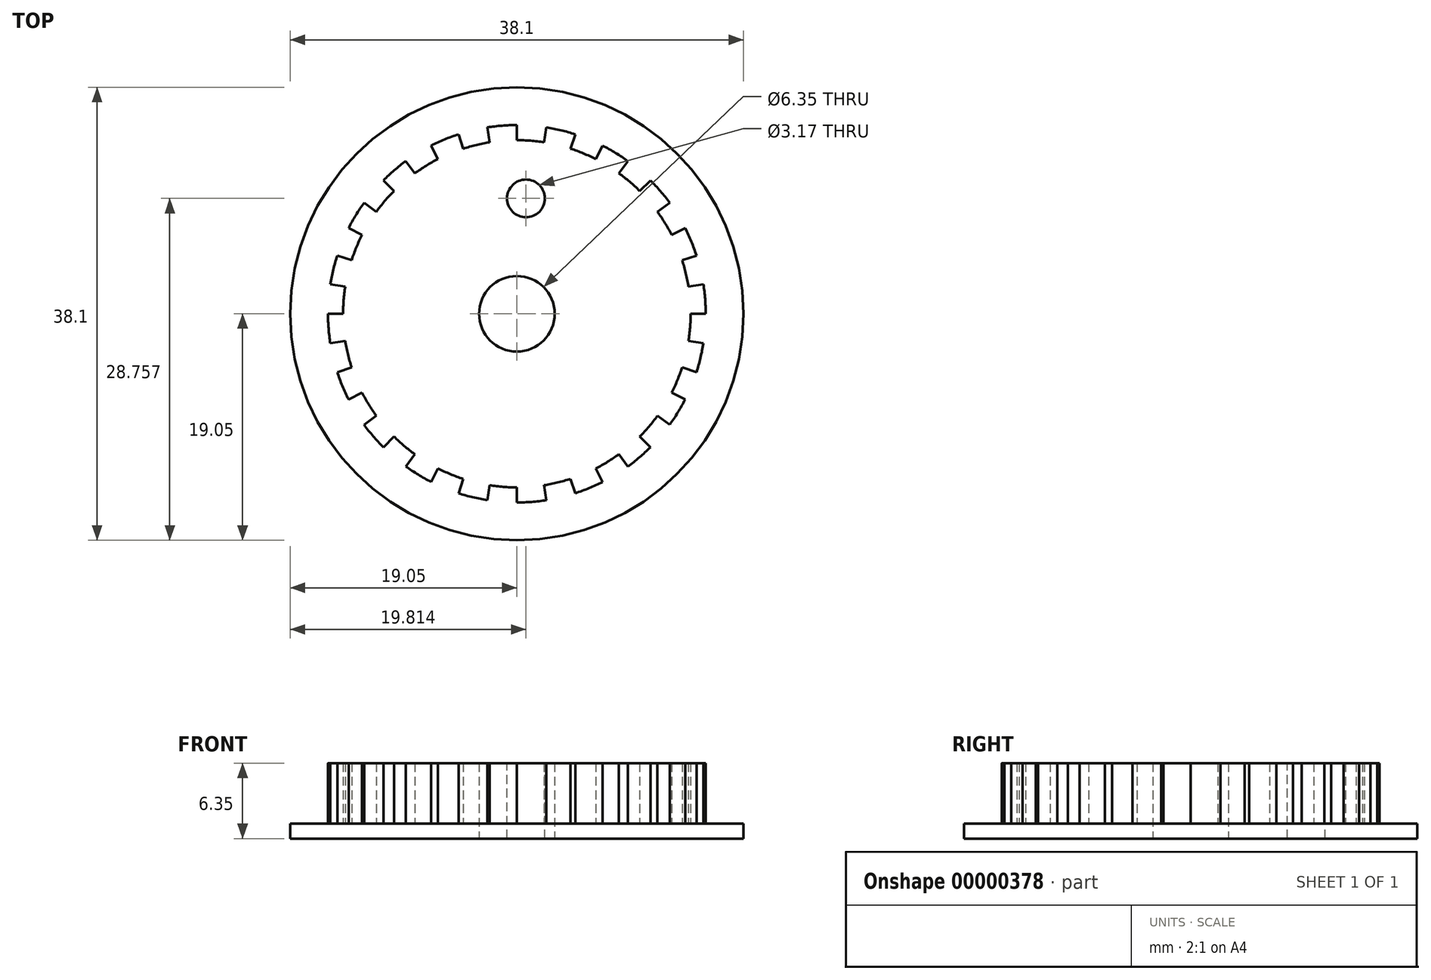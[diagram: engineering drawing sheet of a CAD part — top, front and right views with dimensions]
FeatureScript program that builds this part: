
annotation { "Feature Type Name" : "Feature", "Feature Type Description" : "" }
export const myFeature = defineFeature(function(context is Context, id is Id, definition is map)
    precondition{}
    {
        {
            var Q0;
            Q0  = qCreatedBy(makeId("Top.planeOp"), FACE);
            var sketch = newSketch(context, id + "F0", { "sketchPlane" : qUnion([Q0])});
            skCircle(sketch, "E0", {"center": v(0, 0) * mm, "radius": 19.05 * mm});
            skCircle(sketch, "E1", {"center": v(0, 0) * mm, "radius": 3.18 * mm});
            skSolve(sketch);
        }
        {
            var Q0;
            Q0=makeQuery(id+"F0.imprint","IMPRINT",FACE,{"disambiguationData":[TD([[makeQuery(id+"F0.imprint","IMPRINT",EDGE,{"derivedFrom":sQuery(id+"F0.wireOp",EDGE,"E0")}),1.0]])]});
            extrude(context, id + "F1", {"entities" : qUnion([Q0]), "depth" : 1.27 * mm});
        }
        {
            var Q0;
            Q0=makeQuery(id+"F1.opExtrude","CAP_FACE",FACE,{"disambiguationData":[OSD([sQuery(id+"F0.wireOp",EDGE,"E0"),sQuery(id+"F0.wireOp",EDGE,"E1")])],"isStart":false});
            var sketch = newSketch(context, id + "F2", { "sketchPlane" : qUnion([Q0])});
            skCircle(sketch, "E2", {"center": v(0, 0) * mm, "radius": 14.6 * mm, "construction": true});
            skCircle(sketch, "E3", {"center": v(0, 0) * mm, "radius": 15.88 * mm, "construction": true});
            skLineSegment(sketch, "E4", {"start": v(0, 0) * mm, "end": v(0, 15.88) * mm, "construction": true});
            skLineSegment(sketch, "E5", {"start": v(0, 0) * mm, "end": v(2.48, 15.68) * mm, "construction": true});
            skLineSegment(sketch, "E6", {"start": v(0, 0) * mm, "end": v(4.9, 15.1) * mm, "construction": true});
            skArc(sketch, "E7", {"start": v(2.28, 14.43) * mm, "mid": v(1.15, 14.56) * mm, "end": v(0, 14.6) * mm});
            skLineSegment(sketch, "E8", {"start": v(2.48, 15.68) * mm, "end": v(2.28, 14.43) * mm});
            skArc(sketch, "E9", {"start": v(4.9, 15.1) * mm, "mid": v(3.7, 15.44) * mm, "end": v(2.48, 15.68) * mm});
            skLineSegment(sketch, "E10", {"start": v(0, 14.6) * mm, "end": v(0, 0) * mm});
            skLineSegment(sketch, "E11", {"start": v(4.9, 15.1) * mm, "end": v(0, 0) * mm});
            skSolve(sketch);
        }
        {
            var Q0;
            {var subQ6=sQuery(id+"F2.wireOp",EDGE,"E7");Q0=makeQuery(id+"F2.imprint","IMPRINT",FACE,{"disambiguationData":[TD([[makeQuery(id+"F2.imprint","IMPRINT",EDGE,{"derivedFrom":subQ6}),1.0]])]});}
            var Q1;
            Q1=sQuery(id+"F2.wireOp",EDGE,"E10");
            var Q2;
            Q2=sQuery(id+"F2.wireOp",EDGE,"E7");
            var Q3;
            Q3=sQuery(id+"F2.wireOp",EDGE,"E8");
            var Q4;
            Q4=sQuery(id+"F2.wireOp",EDGE,"E9");
            var Q5;
            Q5=sQuery(id+"F2.wireOp",EDGE,"E11");
            extrude(context, id + "F3", {"entities" : qUnion([Q0]), "surfaceEntities" : qUnion([Q1, Q2, Q3, Q4, Q5]), "depth" : 5.08 * mm});
        }
        {
            var Q0;
            Q0  = qCreatedBy(makeId("Front.planeOp"), FACE);
            var sketch = newSketch(context, id + "F4", { "sketchPlane" : qUnion([Q0])});
            skLineSegment(sketch, "E12", {"start": v(0, 0) * mm, "end": v(0, 20.74) * mm, "construction": true});
            skSolve(sketch);
        }
        {
            var Q0;
            Q0=makeQuery(id+"F3.opExtrude","SWEPT_BODY",BODY,{"disambiguationData":[OSD([sQuery(id+"F0.wireOp",EDGE,"E1"),sQuery(id+"F2.wireOp",EDGE,"E7"),sQuery(id+"F2.wireOp",EDGE,"E8"),sQuery(id+"F2.wireOp",EDGE,"E9"),sQuery(id+"F2.wireOp",EDGE,"E10"),sQuery(id+"F2.wireOp",EDGE,"E11")])]});
            var Q1;
            Q1=sQuery(id+"F4.wireOp",EDGE,"E12");
            circularPattern(context, id + "F5", {"entities" : qUnion([Q0]), "axis" : qUnion([Q1]), "angle" : 18 * degree, "instanceCount" : 20});
        }
        {
            var Q0;
            Q0=makeQuery(id+"F1.opExtrude","SWEPT_BODY",BODY,{"disambiguationData":[OSD([sQuery(id+"F0.wireOp",EDGE,"E0"),sQuery(id+"F0.wireOp",EDGE,"E1")])]});
            var Q1;
            Q1=makeQuery(id+"F5.opPattern","COPY",BODY,{"derivedFrom":makeQuery(id+"F3.opExtrude","SWEPT_BODY",BODY,{"disambiguationData":[OSD([sQuery(id+"F0.wireOp",EDGE,"E1"),sQuery(id+"F2.wireOp",EDGE,"E7"),sQuery(id+"F2.wireOp",EDGE,"E8"),sQuery(id+"F2.wireOp",EDGE,"E9"),sQuery(id+"F2.wireOp",EDGE,"E10"),sQuery(id+"F2.wireOp",EDGE,"E11")])]}),"instanceName":"4"});
            var Q2;
            Q2=makeQuery(id+"F5.opPattern","COPY",BODY,{"derivedFrom":makeQuery(id+"F3.opExtrude","SWEPT_BODY",BODY,{"disambiguationData":[OSD([sQuery(id+"F0.wireOp",EDGE,"E1"),sQuery(id+"F2.wireOp",EDGE,"E7"),sQuery(id+"F2.wireOp",EDGE,"E8"),sQuery(id+"F2.wireOp",EDGE,"E9"),sQuery(id+"F2.wireOp",EDGE,"E10"),sQuery(id+"F2.wireOp",EDGE,"E11")])]}),"instanceName":"3"});
            var Q3;
            Q3=makeQuery(id+"F5.opPattern","COPY",BODY,{"derivedFrom":makeQuery(id+"F3.opExtrude","SWEPT_BODY",BODY,{"disambiguationData":[OSD([sQuery(id+"F0.wireOp",EDGE,"E1"),sQuery(id+"F2.wireOp",EDGE,"E7"),sQuery(id+"F2.wireOp",EDGE,"E8"),sQuery(id+"F2.wireOp",EDGE,"E9"),sQuery(id+"F2.wireOp",EDGE,"E10"),sQuery(id+"F2.wireOp",EDGE,"E11")])]}),"instanceName":"2"});
            var Q4;
            Q4=makeQuery(id+"F5.opPattern","COPY",BODY,{"derivedFrom":makeQuery(id+"F3.opExtrude","SWEPT_BODY",BODY,{"disambiguationData":[OSD([sQuery(id+"F0.wireOp",EDGE,"E1"),sQuery(id+"F2.wireOp",EDGE,"E7"),sQuery(id+"F2.wireOp",EDGE,"E8"),sQuery(id+"F2.wireOp",EDGE,"E9"),sQuery(id+"F2.wireOp",EDGE,"E10"),sQuery(id+"F2.wireOp",EDGE,"E11")])]}),"instanceName":"1"});
            var Q5;
            Q5=makeQuery(id+"F3.opExtrude","SWEPT_BODY",BODY,{"disambiguationData":[OSD([sQuery(id+"F0.wireOp",EDGE,"E1"),sQuery(id+"F2.wireOp",EDGE,"E7"),sQuery(id+"F2.wireOp",EDGE,"E8"),sQuery(id+"F2.wireOp",EDGE,"E9"),sQuery(id+"F2.wireOp",EDGE,"E10"),sQuery(id+"F2.wireOp",EDGE,"E11")])]});
            var Q6;
            Q6=makeQuery(id+"F5.opPattern","COPY",BODY,{"derivedFrom":makeQuery(id+"F3.opExtrude","SWEPT_BODY",BODY,{"disambiguationData":[OSD([sQuery(id+"F0.wireOp",EDGE,"E1"),sQuery(id+"F2.wireOp",EDGE,"E7"),sQuery(id+"F2.wireOp",EDGE,"E8"),sQuery(id+"F2.wireOp",EDGE,"E9"),sQuery(id+"F2.wireOp",EDGE,"E10"),sQuery(id+"F2.wireOp",EDGE,"E11")])]}),"instanceName":"19"});
            var Q7;
            Q7=makeQuery(id+"F5.opPattern","COPY",BODY,{"derivedFrom":makeQuery(id+"F3.opExtrude","SWEPT_BODY",BODY,{"disambiguationData":[OSD([sQuery(id+"F0.wireOp",EDGE,"E1"),sQuery(id+"F2.wireOp",EDGE,"E7"),sQuery(id+"F2.wireOp",EDGE,"E8"),sQuery(id+"F2.wireOp",EDGE,"E9"),sQuery(id+"F2.wireOp",EDGE,"E10"),sQuery(id+"F2.wireOp",EDGE,"E11")])]}),"instanceName":"18"});
            var Q8;
            Q8=makeQuery(id+"F5.opPattern","COPY",BODY,{"derivedFrom":makeQuery(id+"F3.opExtrude","SWEPT_BODY",BODY,{"disambiguationData":[OSD([sQuery(id+"F0.wireOp",EDGE,"E1"),sQuery(id+"F2.wireOp",EDGE,"E7"),sQuery(id+"F2.wireOp",EDGE,"E8"),sQuery(id+"F2.wireOp",EDGE,"E9"),sQuery(id+"F2.wireOp",EDGE,"E10"),sQuery(id+"F2.wireOp",EDGE,"E11")])]}),"instanceName":"17"});
            var Q9;
            Q9=makeQuery(id+"F5.opPattern","COPY",BODY,{"derivedFrom":makeQuery(id+"F3.opExtrude","SWEPT_BODY",BODY,{"disambiguationData":[OSD([sQuery(id+"F0.wireOp",EDGE,"E1"),sQuery(id+"F2.wireOp",EDGE,"E7"),sQuery(id+"F2.wireOp",EDGE,"E8"),sQuery(id+"F2.wireOp",EDGE,"E9"),sQuery(id+"F2.wireOp",EDGE,"E10"),sQuery(id+"F2.wireOp",EDGE,"E11")])]}),"instanceName":"16"});
            var Q10;
            Q10=makeQuery(id+"F5.opPattern","COPY",BODY,{"derivedFrom":makeQuery(id+"F3.opExtrude","SWEPT_BODY",BODY,{"disambiguationData":[OSD([sQuery(id+"F0.wireOp",EDGE,"E1"),sQuery(id+"F2.wireOp",EDGE,"E7"),sQuery(id+"F2.wireOp",EDGE,"E8"),sQuery(id+"F2.wireOp",EDGE,"E9"),sQuery(id+"F2.wireOp",EDGE,"E10"),sQuery(id+"F2.wireOp",EDGE,"E11")])]}),"instanceName":"15"});
            var Q11;
            Q11=makeQuery(id+"F5.opPattern","COPY",BODY,{"derivedFrom":makeQuery(id+"F3.opExtrude","SWEPT_BODY",BODY,{"disambiguationData":[OSD([sQuery(id+"F0.wireOp",EDGE,"E1"),sQuery(id+"F2.wireOp",EDGE,"E7"),sQuery(id+"F2.wireOp",EDGE,"E8"),sQuery(id+"F2.wireOp",EDGE,"E9"),sQuery(id+"F2.wireOp",EDGE,"E10"),sQuery(id+"F2.wireOp",EDGE,"E11")])]}),"instanceName":"14"});
            var Q12;
            Q12=makeQuery(id+"F5.opPattern","COPY",BODY,{"derivedFrom":makeQuery(id+"F3.opExtrude","SWEPT_BODY",BODY,{"disambiguationData":[OSD([sQuery(id+"F0.wireOp",EDGE,"E1"),sQuery(id+"F2.wireOp",EDGE,"E7"),sQuery(id+"F2.wireOp",EDGE,"E8"),sQuery(id+"F2.wireOp",EDGE,"E9"),sQuery(id+"F2.wireOp",EDGE,"E10"),sQuery(id+"F2.wireOp",EDGE,"E11")])]}),"instanceName":"13"});
            var Q13;
            Q13=makeQuery(id+"F5.opPattern","COPY",BODY,{"derivedFrom":makeQuery(id+"F3.opExtrude","SWEPT_BODY",BODY,{"disambiguationData":[OSD([sQuery(id+"F0.wireOp",EDGE,"E1"),sQuery(id+"F2.wireOp",EDGE,"E7"),sQuery(id+"F2.wireOp",EDGE,"E8"),sQuery(id+"F2.wireOp",EDGE,"E9"),sQuery(id+"F2.wireOp",EDGE,"E10"),sQuery(id+"F2.wireOp",EDGE,"E11")])]}),"instanceName":"12"});
            var Q14;
            Q14=makeQuery(id+"F5.opPattern","COPY",BODY,{"derivedFrom":makeQuery(id+"F3.opExtrude","SWEPT_BODY",BODY,{"disambiguationData":[OSD([sQuery(id+"F0.wireOp",EDGE,"E1"),sQuery(id+"F2.wireOp",EDGE,"E7"),sQuery(id+"F2.wireOp",EDGE,"E8"),sQuery(id+"F2.wireOp",EDGE,"E9"),sQuery(id+"F2.wireOp",EDGE,"E10"),sQuery(id+"F2.wireOp",EDGE,"E11")])]}),"instanceName":"11"});
            var Q15;
            Q15=makeQuery(id+"F5.opPattern","COPY",BODY,{"derivedFrom":makeQuery(id+"F3.opExtrude","SWEPT_BODY",BODY,{"disambiguationData":[OSD([sQuery(id+"F0.wireOp",EDGE,"E1"),sQuery(id+"F2.wireOp",EDGE,"E7"),sQuery(id+"F2.wireOp",EDGE,"E8"),sQuery(id+"F2.wireOp",EDGE,"E9"),sQuery(id+"F2.wireOp",EDGE,"E10"),sQuery(id+"F2.wireOp",EDGE,"E11")])]}),"instanceName":"10"});
            var Q16;
            Q16=makeQuery(id+"F5.opPattern","COPY",BODY,{"derivedFrom":makeQuery(id+"F3.opExtrude","SWEPT_BODY",BODY,{"disambiguationData":[OSD([sQuery(id+"F0.wireOp",EDGE,"E1"),sQuery(id+"F2.wireOp",EDGE,"E7"),sQuery(id+"F2.wireOp",EDGE,"E8"),sQuery(id+"F2.wireOp",EDGE,"E9"),sQuery(id+"F2.wireOp",EDGE,"E10"),sQuery(id+"F2.wireOp",EDGE,"E11")])]}),"instanceName":"9"});
            var Q17;
            Q17=makeQuery(id+"F5.opPattern","COPY",BODY,{"derivedFrom":makeQuery(id+"F3.opExtrude","SWEPT_BODY",BODY,{"disambiguationData":[OSD([sQuery(id+"F0.wireOp",EDGE,"E1"),sQuery(id+"F2.wireOp",EDGE,"E7"),sQuery(id+"F2.wireOp",EDGE,"E8"),sQuery(id+"F2.wireOp",EDGE,"E9"),sQuery(id+"F2.wireOp",EDGE,"E10"),sQuery(id+"F2.wireOp",EDGE,"E11")])]}),"instanceName":"8"});
            var Q18;
            Q18=makeQuery(id+"F5.opPattern","COPY",BODY,{"derivedFrom":makeQuery(id+"F3.opExtrude","SWEPT_BODY",BODY,{"disambiguationData":[OSD([sQuery(id+"F0.wireOp",EDGE,"E1"),sQuery(id+"F2.wireOp",EDGE,"E7"),sQuery(id+"F2.wireOp",EDGE,"E8"),sQuery(id+"F2.wireOp",EDGE,"E9"),sQuery(id+"F2.wireOp",EDGE,"E10"),sQuery(id+"F2.wireOp",EDGE,"E11")])]}),"instanceName":"7"});
            var Q19;
            Q19=makeQuery(id+"F5.opPattern","COPY",BODY,{"derivedFrom":makeQuery(id+"F3.opExtrude","SWEPT_BODY",BODY,{"disambiguationData":[OSD([sQuery(id+"F0.wireOp",EDGE,"E1"),sQuery(id+"F2.wireOp",EDGE,"E7"),sQuery(id+"F2.wireOp",EDGE,"E8"),sQuery(id+"F2.wireOp",EDGE,"E9"),sQuery(id+"F2.wireOp",EDGE,"E10"),sQuery(id+"F2.wireOp",EDGE,"E11")])]}),"instanceName":"6"});
            var Q20;
            Q20=makeQuery(id+"F5.opPattern","COPY",BODY,{"derivedFrom":makeQuery(id+"F3.opExtrude","SWEPT_BODY",BODY,{"disambiguationData":[OSD([sQuery(id+"F0.wireOp",EDGE,"E1"),sQuery(id+"F2.wireOp",EDGE,"E7"),sQuery(id+"F2.wireOp",EDGE,"E8"),sQuery(id+"F2.wireOp",EDGE,"E9"),sQuery(id+"F2.wireOp",EDGE,"E10"),sQuery(id+"F2.wireOp",EDGE,"E11")])]}),"instanceName":"5"});
            booleanBodies(context, id + "F6", {"operationType" : BooleanOperationType.UNION, "tools" : qUnion([Q0, Q1, Q2, Q3, Q4, Q5, Q6, Q7, Q8, Q9, Q10, Q11, Q12, Q13, Q14, Q15, Q16, Q17, Q18, Q19, Q20])});
        }
        {
            var Q0;
            {var subQ0=makeQuery(id+"F3.opExtrude","CAP_FACE",FACE,{"disambiguationData":[OSD([sQuery(id+"F0.wireOp",EDGE,"E1"),sQuery(id+"F2.wireOp",EDGE,"E7"),sQuery(id+"F2.wireOp",EDGE,"E8"),sQuery(id+"F2.wireOp",EDGE,"E9"),sQuery(id+"F2.wireOp",EDGE,"E10"),sQuery(id+"F2.wireOp",EDGE,"E11")])],"isStart":false});Q0=makeQuery(id+"F6.opBoolean","MERGE",FACE,{"derivedFrom":[subQ0,makeQuery(id+"F5.opPattern","COPY",FACE,{"derivedFrom":subQ0,"instanceName":"1"}),makeQuery(id+"F5.opPattern","COPY",FACE,{"derivedFrom":subQ0,"instanceName":"2"}),makeQuery(id+"F5.opPattern","COPY",FACE,{"derivedFrom":subQ0,"instanceName":"3"}),makeQuery(id+"F5.opPattern","COPY",FACE,{"derivedFrom":subQ0,"instanceName":"4"}),makeQuery(id+"F5.opPattern","COPY",FACE,{"derivedFrom":subQ0,"instanceName":"5"}),makeQuery(id+"F5.opPattern","COPY",FACE,{"derivedFrom":subQ0,"instanceName":"6"}),makeQuery(id+"F5.opPattern","COPY",FACE,{"derivedFrom":subQ0,"instanceName":"7"}),makeQuery(id+"F5.opPattern","COPY",FACE,{"derivedFrom":subQ0,"instanceName":"8"}),makeQuery(id+"F5.opPattern","COPY",FACE,{"derivedFrom":subQ0,"instanceName":"9"}),makeQuery(id+"F5.opPattern","COPY",FACE,{"derivedFrom":subQ0,"instanceName":"10"}),makeQuery(id+"F5.opPattern","COPY",FACE,{"derivedFrom":subQ0,"instanceName":"11"}),makeQuery(id+"F5.opPattern","COPY",FACE,{"derivedFrom":subQ0,"instanceName":"12"}),makeQuery(id+"F5.opPattern","COPY",FACE,{"derivedFrom":subQ0,"instanceName":"13"}),makeQuery(id+"F5.opPattern","COPY",FACE,{"derivedFrom":subQ0,"instanceName":"14"}),makeQuery(id+"F5.opPattern","COPY",FACE,{"derivedFrom":subQ0,"instanceName":"15"}),makeQuery(id+"F5.opPattern","COPY",FACE,{"derivedFrom":subQ0,"instanceName":"16"}),makeQuery(id+"F5.opPattern","COPY",FACE,{"derivedFrom":subQ0,"instanceName":"17"}),makeQuery(id+"F5.opPattern","COPY",FACE,{"derivedFrom":subQ0,"instanceName":"18"}),makeQuery(id+"F5.opPattern","COPY",FACE,{"derivedFrom":subQ0,"instanceName":"19"})]});}
            var sketch = newSketch(context, id + "F7", { "sketchPlane" : qUnion([Q0])});
            skCircle(sketch, "E13", {"center": v(0.76, 9.7) * mm, "radius": 1.59 * mm});
            skLineSegment(sketch, "E14", {"start": v(0, 0) * mm, "end": v(0.38, 4.85) * mm, "construction": true});
            skLineSegment(sketch, "E15", {"start": v(0.38, 4.85) * mm, "end": v(0.76, 9.7) * mm, "construction": true});
            skLineSegment(sketch, "E16", {"start": v(0.76, 9.7) * mm, "end": v(1.15, 14.56) * mm, "construction": true});
            skSolve(sketch);
        }
        {
            var Q0;
            Q0=makeQuery(id+"F7.imprint","IMPRINT",FACE,{"disambiguationData":[TD([[makeQuery(id+"F7.imprint","IMPRINT",EDGE,{"derivedFrom":sQuery(id+"F7.wireOp",EDGE,"E13")}),1.0]])]});
            var Q1;
            Q1=sQuery(id+"F7.wireOp",EDGE,"E13");
            extrude(context, id + "F8", {"entities" : qUnion([Q0]), "operationType" : NewBodyOperationType.REMOVE, "surfaceEntities" : qUnion([Q1]), "oppositeDirection" : true, "depth" : 6.35 * mm});
        }
    });
